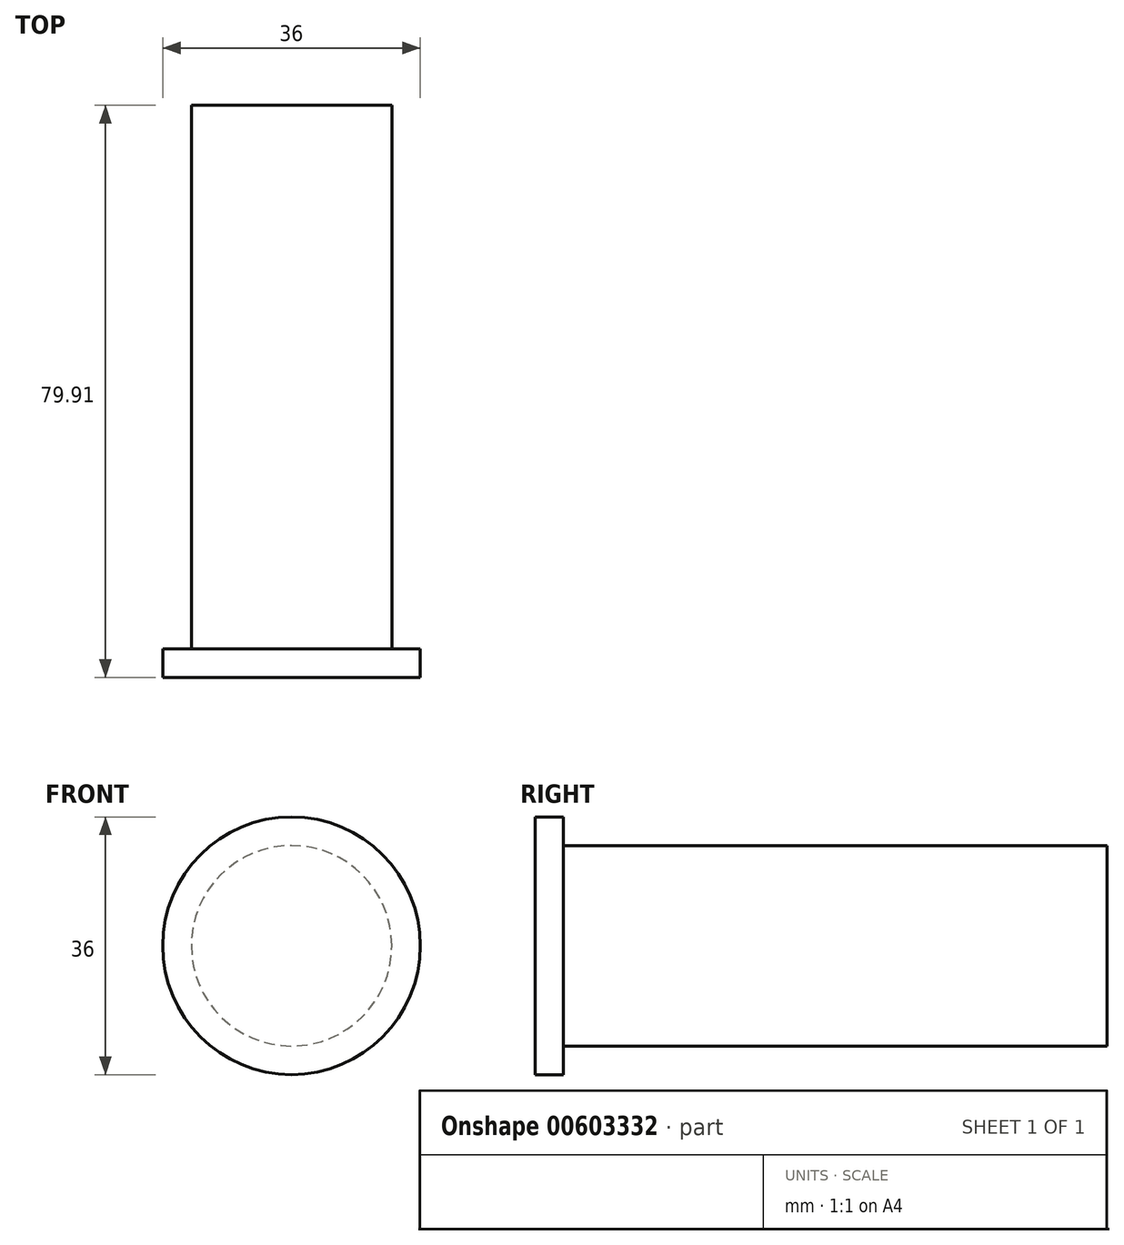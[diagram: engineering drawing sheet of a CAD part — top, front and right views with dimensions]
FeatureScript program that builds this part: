
annotation { "Feature Type Name" : "Feature", "Feature Type Description" : "" }
export const myFeature = defineFeature(function(context is Context, id is Id, definition is map)
    precondition{}
    {
        {
            var Q0;
            Q0=qCreatedBy(makeId("Front.planeOp"),FACE);
            var sketch = newSketch(context, id + "F0", { "sketchPlane" : qUnion([Q0])});
            skCircle(sketch, "E0", {"center": v(0, 0) * mm, "radius": 14 * mm});
            skPoint(sketch, "E1", {"position": v(0, 26) * mm});
            skFitSpline(sketch, "E2", {"points": [v(-14, 0) * mm, v(0, 26) * mm, v(14, 0) * mm, v(0, -14) * mm, v(-14, 0) * mm]});
            skSolve(sketch);
        }
        {
            var Q0;
            {var subQ0=sQuery(id+"F0.wireOp",EDGE,"E2");var subQ1=sQuery(id+"F0.wireOp",EDGE,"E0");var subQ2=makeQuery(id+"F0.imprint","INTERSECT",VERTEX,{"disambiguationData":[OD(0.0)],"derivedFrom":[subQ1,subQ0]});Q0=makeQuery(id+"F0.imprint","IMPRINT",FACE,{"disambiguationData":[TD([[makeQuery(id+"F0.imprint","IMPRINT",EDGE,{"disambiguationData":[TD([[subQ2,1.0]])],"derivedFrom":subQ1}),-1.0]])]});}
            var Q1;
            {var subQ0=sQuery(id+"F0.wireOp",EDGE,"E2");var subQ1=sQuery(id+"F0.wireOp",EDGE,"E0");var subQ2=makeQuery(id+"F0.imprint","INTERSECT",VERTEX,{"disambiguationData":[OD(0.0)],"derivedFrom":[subQ1,subQ0]});Q1=makeQuery(id+"F0.imprint","IMPRINT",FACE,{"disambiguationData":[TD([[makeQuery(id+"F0.imprint","IMPRINT",EDGE,{"disambiguationData":[TD([[subQ2,1.0]])],"derivedFrom":subQ1}),1.0]])]});}
            var Q2;
            {var subQ0=sQuery(id+"F0.wireOp",EDGE,"E2");var subQ1=sQuery(id+"F0.wireOp",EDGE,"E0");var subQ2=makeQuery(id+"F0.imprint","INTERSECT",VERTEX,{"disambiguationData":[OD(0.0)],"derivedFrom":[subQ1,subQ0]});Q2=makeQuery(id+"F0.imprint","IMPRINT",FACE,{"disambiguationData":[TD([[makeQuery(id+"F0.imprint","IMPRINT",EDGE,{"disambiguationData":[TD([[subQ2,-1.0]])],"derivedFrom":subQ1}),1.0]])]});}
            var Q3;
            {var subQ0=sQuery(id+"F0.wireOp",EDGE,"E2");var subQ1=sQuery(id+"F0.wireOp",EDGE,"E0");var subQ2=makeQuery(id+"F0.imprint","INTERSECT",VERTEX,{"disambiguationData":[OD(1.0)],"derivedFrom":[subQ1,subQ0]});Q3=makeQuery(id+"F0.imprint","IMPRINT",FACE,{"disambiguationData":[TD([[makeQuery(id+"F0.imprint","IMPRINT",EDGE,{"disambiguationData":[TD([[subQ2,1.0]])],"derivedFrom":subQ1}),1.0]])]});}
            extrude(context, id + "F1", {"entities" : qUnion([Q0, Q1, Q2, Q3]), "oppositeDirection" : true, "depth" : 15 * mm, "offsetDistance" : 25 * mm});
        }
        {
            var Q0;
            {var subQ0=sQuery(id+"F0.wireOp",EDGE,"E2");var subQ1=sQuery(id+"F0.wireOp",EDGE,"E0");var subQ2=makeQuery(id+"F0.imprint","INTERSECT",VERTEX,{"disambiguationData":[OD(1.0)],"derivedFrom":[subQ1,subQ0]});Q0=makeQuery(id+"F0.imprint","IMPRINT",FACE,{"disambiguationData":[TD([[makeQuery(id+"F0.imprint","IMPRINT",EDGE,{"disambiguationData":[TD([[subQ2,1.0]])],"derivedFrom":subQ1}),1.0]])]});}
            var Q1;
            {var subQ0=sQuery(id+"F0.wireOp",EDGE,"E2");var subQ1=sQuery(id+"F0.wireOp",EDGE,"E0");var subQ2=makeQuery(id+"F0.imprint","INTERSECT",VERTEX,{"disambiguationData":[OD(0.0)],"derivedFrom":[subQ1,subQ0]});Q1=makeQuery(id+"F0.imprint","IMPRINT",FACE,{"disambiguationData":[TD([[makeQuery(id+"F0.imprint","IMPRINT",EDGE,{"disambiguationData":[TD([[subQ2,1.0]])],"derivedFrom":subQ1}),1.0]])]});}
            var Q2;
            {var subQ0=sQuery(id+"F0.wireOp",EDGE,"E2");var subQ1=sQuery(id+"F0.wireOp",EDGE,"E0");var subQ2=makeQuery(id+"F0.imprint","INTERSECT",VERTEX,{"disambiguationData":[OD(0.0)],"derivedFrom":[subQ1,subQ0]});Q2=makeQuery(id+"F0.imprint","IMPRINT",FACE,{"disambiguationData":[TD([[makeQuery(id+"F0.imprint","IMPRINT",EDGE,{"disambiguationData":[TD([[subQ2,-1.0]])],"derivedFrom":subQ1}),1.0]])]});}
            extrude(context, id + "F2", {"entities" : qUnion([Q0, Q1, Q2]), "operationType" : NewBodyOperationType.ADD, "depth" : ((58.2 + (15.4 / 2)) - 5) * mm, "offsetDistance" : 25 * mm});
        }
        {
            var Q0;
            Q0=makeQuery(id+"F2.opExtrude","CAP_FACE",FACE,{"disambiguationData":[OSD([sQuery(id+"F0.wireOp",EDGE,"E0")])],"isStart":false});
            var sketch = newSketch(context, id + "F3", { "sketchPlane" : qUnion([Q0])});
            skCircle(sketch, "E3", {"center": v(0, 0) * mm, "radius": 18 * mm});
            skSolve(sketch);
        }
        {
            var Q0;
            Q0=makeQuery(id+"F3.imprint","IMPRINT",FACE,{"disambiguationData":[TD([[makeQuery(id+"F3.imprint","IMPRINT",EDGE,{"derivedFrom":makeQuery(id+"F2.opExtrude","CAP_EDGE",EDGE,{"disambiguationData":[OSD([sQuery(id+"F0.wireOp",EDGE,"E0")])],"isStart":false})}),1.0]])]});
            var Q1;
            Q1=makeQuery(id+"F3.imprint","IMPRINT",FACE,{"disambiguationData":[TD([[makeQuery(id+"F3.imprint","IMPRINT",EDGE,{"derivedFrom":sQuery(id+"F3.wireOp",EDGE,"E3")}),1.0]])]});
            extrude(context, id + "F4", {"entities" : qUnion([Q0, Q1]), "operationType" : NewBodyOperationType.ADD, "depth" : 4 * mm, "offsetDistance" : 25 * mm});
        }
    });
